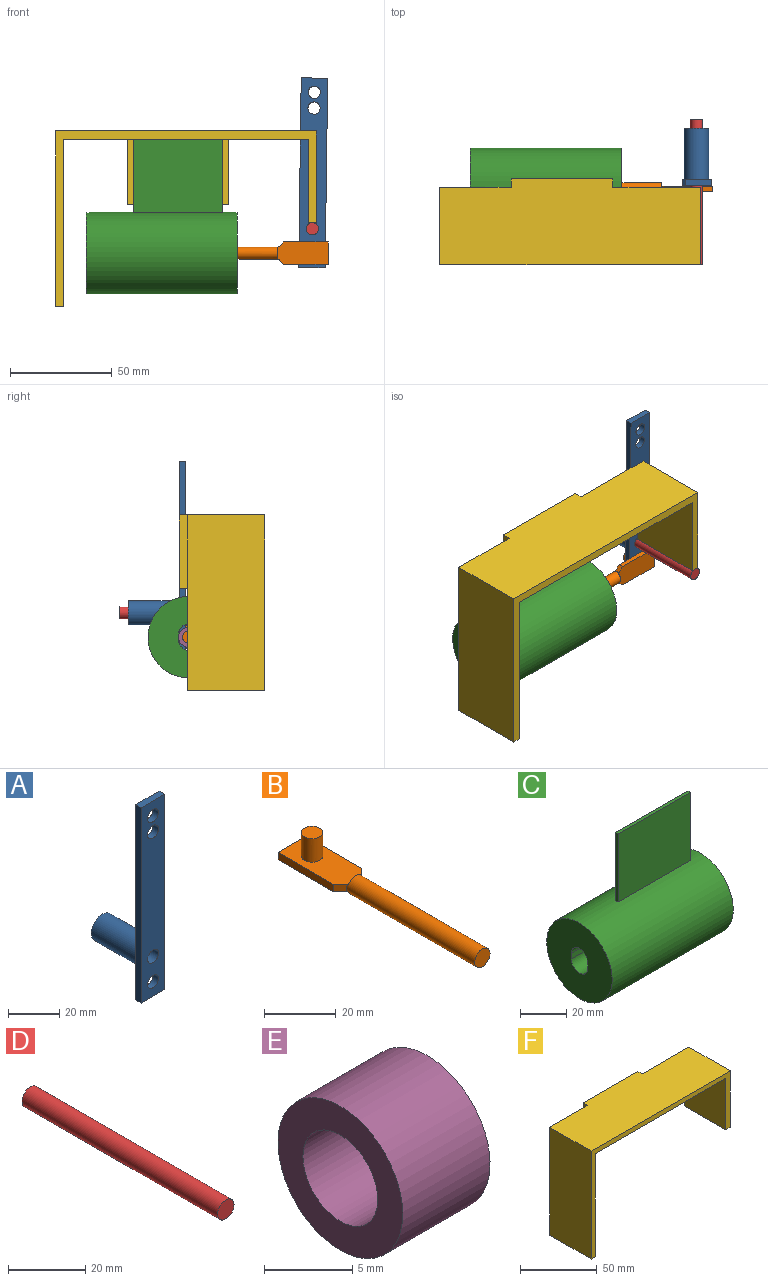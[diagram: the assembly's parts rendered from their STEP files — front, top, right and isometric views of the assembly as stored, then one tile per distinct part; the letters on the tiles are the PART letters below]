
ASSEMBLY  parts=6 mates=6
PART A: 12 faces, bbox 13x28x93 mm
  f0: plane 93x3mm, normal (1,0,0), area 279mm2, adj f1,f6,f8,f9
  f1: plane 13x3mm, normal (0,0,1), area 39mm2, adj f0,f2,f8,f9
  f2: plane 93x3mm, normal (-1,0,0), area 279mm2, adj f1,f6,f8,f9
  f3: cylinder r=3mm len=6mm, axis (0,1,0), area 56.5mm2, adj f8,f9
  f4: cylinder r=3mm len=6mm, axis (0,1,0), area 56.5mm2, adj f8,f9
  f5: cylinder r=3mm len=6mm, axis (0,1,0), area 56.5mm2, adj f8,f9
  f6: plane 13x3mm, normal (0,0,-1), area 39mm2, adj f0,f2,f8,f9
  f7: cylinder r=3mm len=28mm, axis (0,1,0), area 527.8mm2, adj f8,f11
  f8: plane 93x13mm, normal (0,-1,0), area 1095.9mm2, adj f0,f1,f2,f3,f4,f5,f6,f7
  f9: plane 93x13mm, normal (0,1,0), area 1011.1mm2, adj f0,f1,f2,f3,f4,f5,f6,f10
  f10: cylinder r=6mm len=25mm, axis (0,-1,0), area 942.5mm2, adj f9,f11
  f11: plane 12x12mm, normal (0,1,0), area 84.8mm2, adj f7,f10
PART B: 13 faces, bbox 11x75x12.3 mm
  f0: plane 5.45x1.75mm, normal (0,1,0), area 6.9mm2, adj f1,f4
  f1: cylinder r=3mm len=50.5mm, axis (0,1,0), area 944.6mm2, adj f0,f2,f3,f4,f6,f11,f12
  f2: plane 6x6mm, normal (0,-1,0), area 28.3mm2, adj f1
  f3: plane 5.45x1.75mm, normal (0,1,0), area 6.9mm2, adj f1,f6
  f4: plane 25x11mm, normal (0,0,1), area 237.8mm2, adj f0,f1,f5,f7,f8,f9,f11,f12
  f5: plane 22x2.5mm, normal (-1,0,0), area 55mm2, adj f4,f6,f8,f11
  f6: plane 25x11mm, normal (0,0,-1), area 266.1mm2, adj f1,f3,f5,f7,f8,f11,f12
  f7: plane 22x2.5mm, normal (1,0,0), area 55mm2, adj f4,f6,f8,f12
  f8: plane 11x2.5mm, normal (0,1,0), area 27.5mm2, adj f4,f5,f6,f7
  f9: cylinder r=3mm len=8mm, axis (0,0,-1), area 150.8mm2, adj f4,f10
  f10: plane 6x6mm, normal (0,0,1), area 28.3mm2, adj f9
  f11: plane 2.77x2.77mm, normal (-0.71,-0.71,0), area 9.2mm2, adj f1,f4,f5,f6
  f12: plane 2.77x2.77mm, normal (0.71,-0.71,0), area 9.2mm2, adj f1,f4,f6,f7
PART C: 12 faces, bbox 74x40x76 mm
  f0: cylinder r=20mm len=74mm, axis (-1,0,0), area 9238.4mm2, adj f5,f6,f7,f8,f10,f11
  f1: plane 74x3mm, normal (0,1,0), area 222mm2, adj f2,f4,f5,f6
  f2: cylinder r=5mm len=74mm, axis (-1,0,0), area 1162.4mm2, adj f1,f3,f5,f6
  f3: plane 74x3mm, normal (0,-1,0), area 222mm2, adj f2,f4,f5,f6
  f4: cylinder r=5mm len=74mm, axis (-1,0,0), area 1162.4mm2, adj f1,f3,f5,f6
  f5: plane 40x40mm, normal (1,0,0), area 1148.1mm2, adj f0,f1,f2,f3,f4
  f6: plane 40x40mm, normal (-1,0,0), area 1148.1mm2, adj f0,f1,f2,f3,f4
  f7: plane 44x36mm, normal (0,-1,0), area 1584mm2, adj f0,f9,f10,f11
  f8: plane 44x36mm, normal (0,1,0), area 1584mm2, adj f0,f9,f10,f11
  f9: plane 44x1.38mm, normal (0,0,1), area 60.7mm2, adj f7,f8,f10,f11
  f10: plane 36x1.38mm, normal (-1,0,0), area 49.7mm2, adj f0,f7,f8,f9
  f11: plane 36x1.38mm, normal (1,0,0), area 49.7mm2, adj f0,f7,f8,f9
PART D: 3 faces, bbox 6x71.4x6 mm
  f0: cylinder r=3mm len=71.44mm, axis (0,1,0), area 1346.6mm2, adj f1,f2
  f1: plane 6x6mm, normal (0,-1,0), area 28.3mm2, adj f0
  f2: plane 6x6mm, normal (0,1,0), area 28.3mm2, adj f0
PART E: 4 faces, bbox 7x10x10 mm
  f0: plane 10x10mm, normal (1,0,0), area 50.3mm2, adj f2,f3
  f1: plane 10x10mm, normal (-1,0,0), area 50.3mm2, adj f2,f3
  f2: cylinder r=5mm len=10mm, axis (-1,0,0), area 219.9mm2, adj f0,f1
  f3: cylinder r=3mm len=7mm, axis (-1,0,0), area 131.9mm2, adj f0,f1
PART F: 16 faces, bbox 128x42x86 mm
  f0: plane 45x43mm, normal (0,1,0), area 336mm2, adj f1,f5,f8,f9,f10,f14
  f1: plane 120x38mm, normal (0,0,-1), area 4560mm2, adj f0,f4,f6,f7,f9,f12
  f2: plane 86x38mm, normal (-1,0,0), area 3268mm2, adj f3,f5,f6,f7
  f3: plane 38x4mm, normal (0,0,-1), area 152mm2, adj f2,f4,f6,f7
  f4: plane 82x38mm, normal (1,0,0), area 3116mm2, adj f1,f3,f6,f7
  f5: plane 128x42mm, normal (0,0,1), area 5064mm2, adj f0,f2,f6,f7,f8,f11,f14,f15
  f6: plane 128x86mm, normal (0,-1,0), area 1004mm2, adj f1,f2,f3,f4,f5,f8,f9,f10
  f7: plane 86x35mm, normal (0,1,0), area 468mm2, adj f1,f2,f3,f4,f5,f15
  f8: plane 45x38mm, normal (1,0,0), area 1710mm2, adj f0,f5,f6,f10
  f9: plane 41x38mm, normal (-1,0,0), area 1558mm2, adj f0,f1,f6,f10
  f10: plane 38x4mm, normal (0,0,-1), area 152mm2, adj f0,f6,f8,f9
  f11: plane 50x36mm, normal (0,1,0), area 1800mm2, adj f5,f13,f14,f15
  f12: plane 50x32mm, normal (0,-1,0), area 1600mm2, adj f1,f13,f14,f15
  f13: plane 50x4mm, normal (0,0,-1), area 200mm2, adj f11,f12,f14,f15
  f14: plane 36x4mm, normal (1,0,0), area 144mm2, adj f0,f5,f11,f12,f13
  f15: plane 36x4mm, normal (-1,0,0), area 144mm2, adj f5,f7,f11,f12,f13
PLACE A rot(axis=(0,1,0),0.8deg) t=(-10.78,12.54,153.59)mm
PLACE B rot(axis=(-0.58,-0.58,-0.58),120deg) t=(49.87,41.52,25.98)mm
PLACE C t=(19.1,-23.97,41.13)mm
PLACE D t=(-11.79,12.04,152.53)mm
PLACE E rot(axis=(1,0,0),90deg) t=(19.1,33.33,34.64)mm
PLACE F t=(-58.9,8.6,40.53)mm fixed
MATE slider B.f1 <-> E.f2  axis (1,0,0) through (25.27,7.91,66.53)mm
MATE pin_slot E.f2 <-> C.f0  axis (1,0,0) through (30.1,7.91,66.53)mm
MATE revolute A.f7 <-> D.f0  axis (0,1,0) through (67.1,37.54,78.53)mm
MATE fastened F.f12 <-> C.f8  axis (0,-1,0) through (1.1,8.6,122.53)mm
MATE fastened D.f0 <-> F.f6  axis (0,-1,0) through (67.1,-29.4,78.53)mm
MATE cylindrical A.f5 <-> B.f9  axis (0,-1,0) through (66.93,9.54,66.53)mm
